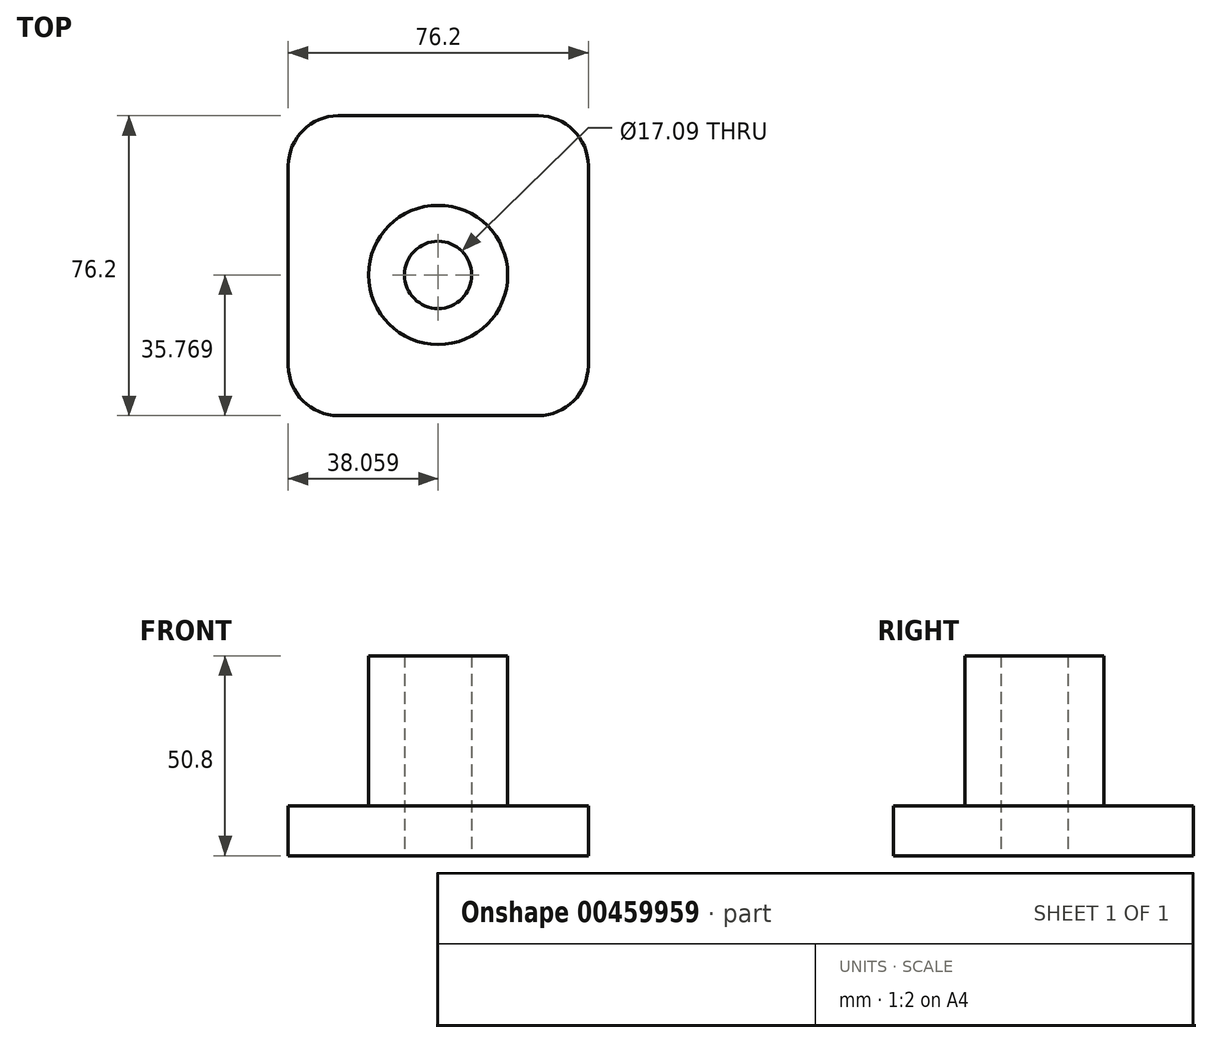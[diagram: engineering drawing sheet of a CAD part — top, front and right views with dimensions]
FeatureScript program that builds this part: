
annotation { "Feature Type Name" : "Feature", "Feature Type Description" : "" }
export const myFeature = defineFeature(function(context is Context, id is Id, definition is map)
    precondition{}
    {
        {
            var Q0;
            Q0=qCreatedBy(makeId("Top.planeOp"),FACE);
            var sketch = newSketch(context, id + "F0", { "sketchPlane" : qUnion([Q0])});
            skLineSegment(sketch, "E0.bottom", {"start": v(-12.7, 0) * mm, "end": v(-63.5, 0) * mm});
            skLineSegment(sketch, "E0.top", {"start": v(-12.7, 76.2) * mm, "end": v(-63.5, 76.2) * mm});
            skLineSegment(sketch, "E0.left", {"start": v(0, 12.7) * mm, "end": v(0, 63.5) * mm});
            skLineSegment(sketch, "E0.right", {"start": v(-76.2, 12.7) * mm, "end": v(-76.2, 63.5) * mm});
            skPoint(sketch, "E1.visualSharp", {"position": v(-76.2, 76.2) * mm});
            skArc(sketch, "E1.filletArc", {"start": v(-63.5, 76.2) * mm, "mid": v(-72.48, 72.48) * mm, "end": v(-76.2, 63.5) * mm});
            skPoint(sketch, "E2.visualSharp", {"position": v(0, 76.2) * mm});
            skArc(sketch, "E2.filletArc", {"start": v(0, 63.5) * mm, "mid": v(-3.72, 72.48) * mm, "end": v(-12.7, 76.2) * mm});
            skPoint(sketch, "E3.visualSharp", {"position": v(0, 0) * mm});
            skArc(sketch, "E3.filletArc", {"start": v(-12.7, 0) * mm, "mid": v(-3.72, 3.72) * mm, "end": v(0, 12.7) * mm});
            skPoint(sketch, "E4.visualSharp", {"position": v(-76.2, 0) * mm});
            skArc(sketch, "E4.filletArc", {"start": v(-76.2, 12.7) * mm, "mid": v(-72.48, 3.72) * mm, "end": v(-63.5, 0) * mm});
            skCircle(sketch, "E5", {"center": v(-38.14, 35.77) * mm, "radius": 17.68 * mm});
            skCircle(sketch, "E6", {"center": v(-38.14, 35.77) * mm, "radius": 8.54 * mm});
            skSolve(sketch);
        }
        {
            var Q0;
            Q0 = qSketchRegion(id + "F0", true);
            extrude(context, id + "F1", {"entities" : qUnion([Q0]), "depth" : 12.7 * mm});
        }
        {
            var Q0;
            Q0=makeQuery(id+"F0.imprint","IMPRINT",FACE,{"disambiguationData":[TD([[makeQuery(id+"F0.imprint","IMPRINT",EDGE,{"derivedFrom":sQuery(id+"F0.wireOp",EDGE,"E5")}),1.0]])]});
            extrude(context, id + "F2", {"entities" : qUnion([Q0]), "operationType" : NewBodyOperationType.ADD, "depth" : 50.8 * mm});
        }
    });
